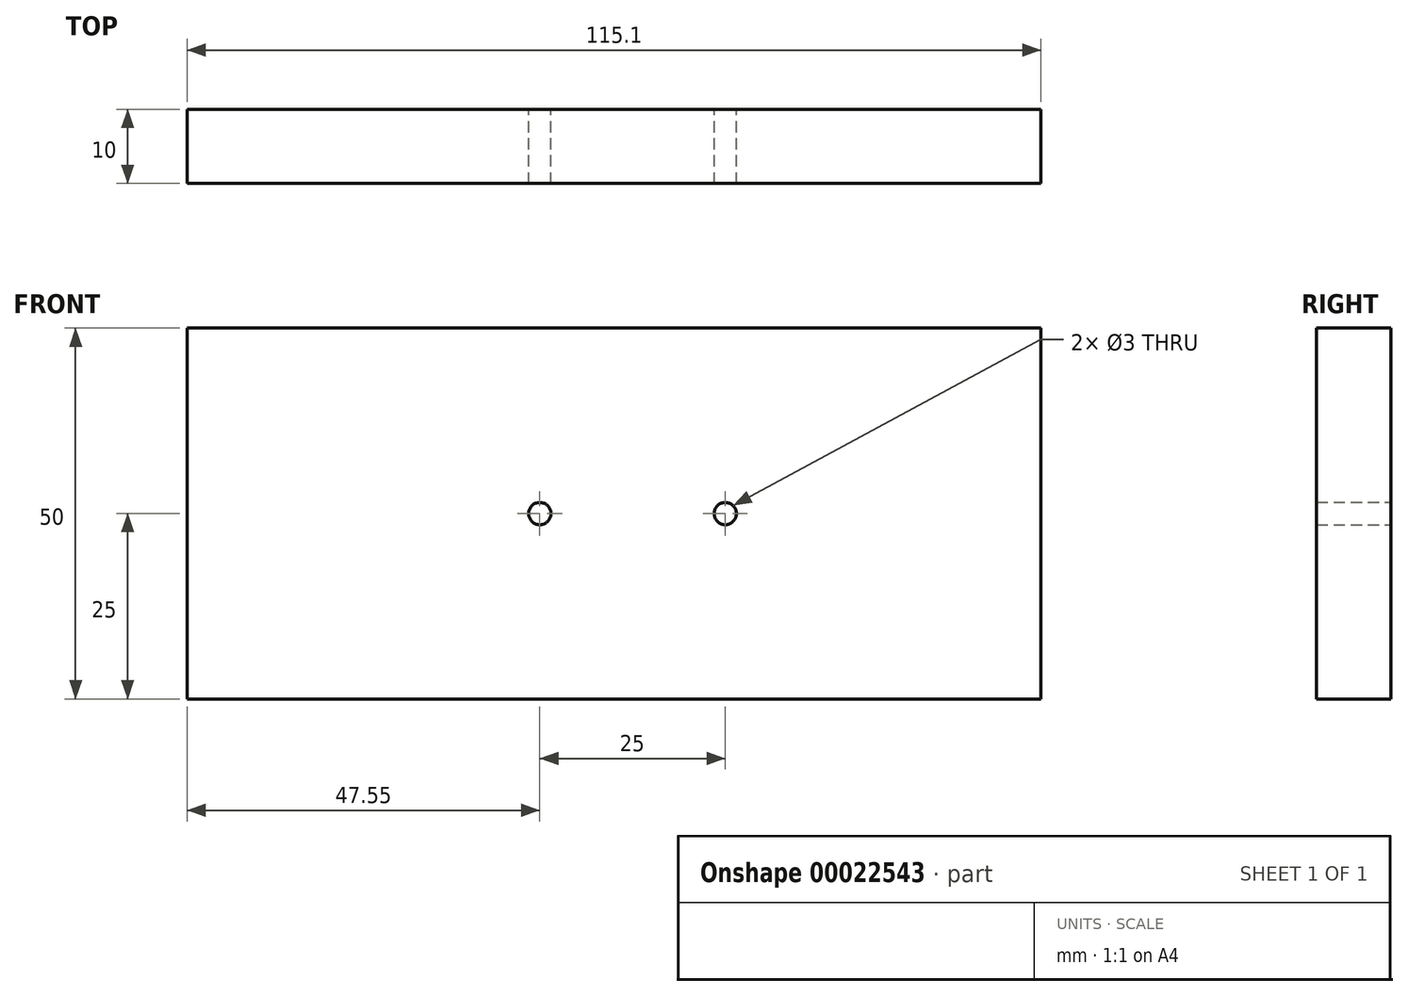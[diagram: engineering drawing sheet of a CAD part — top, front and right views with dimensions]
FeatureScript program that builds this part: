
annotation { "Feature Type Name" : "Feature", "Feature Type Description" : "" }
export const myFeature = defineFeature(function(context is Context, id is Id, definition is map)
    precondition{}
    {
        {
            var Q0;
            Q0=qCreatedBy(makeId("Front.planeOp"),FACE);
            var sketch = newSketch(context, id + "F0", { "sketchPlane" : qUnion([Q0])});
            skLineSegment(sketch, "E0.bottom", {"start": v(-57.55, 25) * mm, "end": v(57.55, 25) * mm});
            skLineSegment(sketch, "E0.top", {"start": v(-57.55, -25) * mm, "end": v(57.55, -25) * mm});
            skLineSegment(sketch, "E0.left", {"start": v(-57.55, 25) * mm, "end": v(-57.55, -25) * mm});
            skLineSegment(sketch, "E0.right", {"start": v(57.55, 25) * mm, "end": v(57.55, -25) * mm});
            skLineSegment(sketch, "E1", {"start": v(0, 0) * mm, "end": v(0, 25) * mm});
            skLineSegment(sketch, "E2", {"start": v(0, 0) * mm, "end": v(0, -25) * mm});
            skCircle(sketch, "E3", {"center": v(-10, 0) * mm, "radius": 1.5 * mm});
            skCircle(sketch, "E4", {"center": v(15, 0) * mm, "radius": 1.5 * mm});
            skLineSegment(sketch, "E5", {"start": v(-10, 0) * mm, "end": v(0, 0) * mm});
            skLineSegment(sketch, "E6", {"start": v(15, 0) * mm, "end": v(0, 0) * mm});
            skSolve(sketch);
        }
        {
            var Q0;
            {var subQ1=sQuery(id+"F0.wireOp",EDGE,"E0.left");Q0=makeQuery(id+"F0.imprint","IMPRINT",FACE,{"disambiguationData":[TD([[makeQuery(id+"F0.imprint","IMPRINT",EDGE,{"derivedFrom":subQ1}),1.0]])]});}
            var Q1;
            {var subQ2=sQuery(id+"F0.wireOp",EDGE,"E0.right");Q1=makeQuery(id+"F0.imprint","IMPRINT",FACE,{"disambiguationData":[TD([[makeQuery(id+"F0.imprint","IMPRINT",EDGE,{"derivedFrom":subQ2}),-1.0]])]});}
            extrude(context, id + "F1", {"entities" : qUnion([Q0, Q1]), "depth" : 10 * mm});
        }
    });
